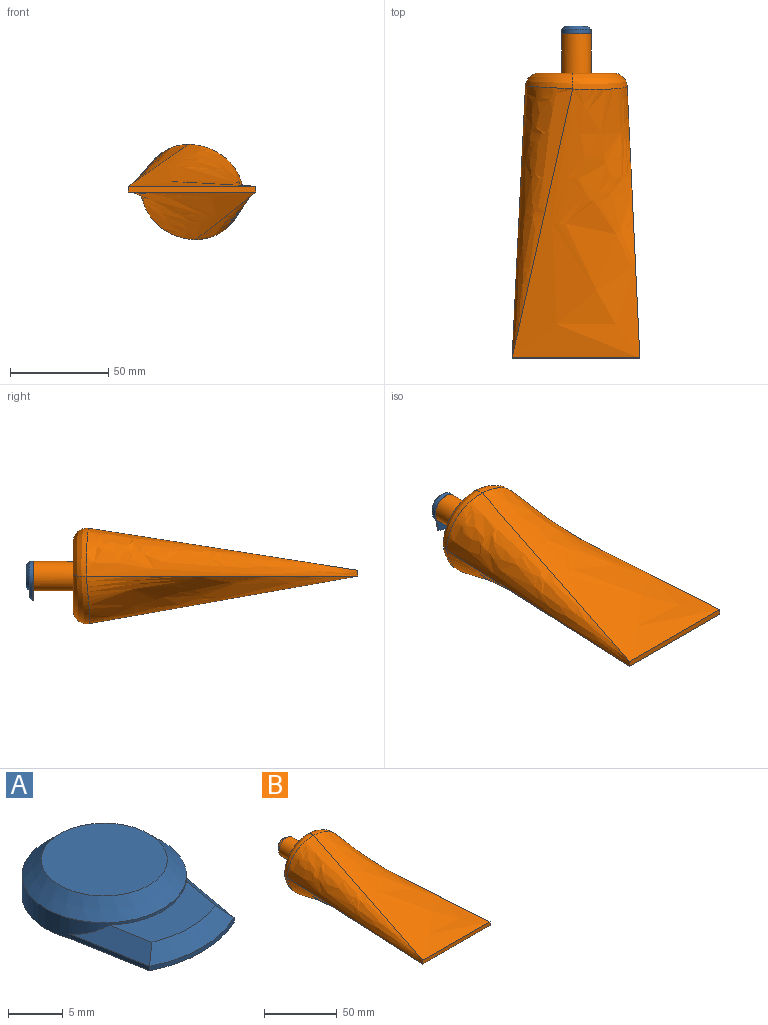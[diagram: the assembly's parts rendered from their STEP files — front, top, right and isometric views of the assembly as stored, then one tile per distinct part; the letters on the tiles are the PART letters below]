
ASSEMBLY  parts=2 mates=1
PART A: 12 faces, bbox 15x20.1x4 mm
  f0: cylinder r=7.5mm len=15mm, axis (0,0,-1), area 97.4mm2, adj f2,f3,f4,f5,f7,f8,f10,f11
  f1: plane 11.5x11.5mm, normal (0,0,1), area 103.9mm2, adj f11
  f2: plane 20.12x15mm, normal (0,0,-1), area 244.3mm2, adj f0,f3,f4,f5,f6
  f3: plane 8.8x1.55mm, normal (-0.98,-0.17,0), area 4.5mm2, adj f0,f2,f6,f10
  f4: plane 8.28x1.46mm, normal (0.98,-0.17,0), area 4.2mm2, adj f0,f2,f6,f8
  f5: cylinder r=7.39mm len=9.81mm, axis (0,0,-1), area 20.9mm2, adj f0,f2,f7,f10
  f6: cylinder r=12.21mm len=10.9mm, axis (0,0,-1), area 5.6mm2, adj f2,f3,f4,f9
  f7: plane 9.84x5.47mm, normal (0,0,1), area 33.7mm2, adj f0,f5,f8,f9,f10
  f8: plane 8.28x2.8mm, normal (0.7,-0.12,0.71), area 13.3mm2, adj f0,f4,f7,f9
  f9: cone r=10.71mm half-angle=45deg, axis (0,0,-1), area 20.9mm2, adj f6,f7,f8,f10
  f10: plane 8.81x2.9mm, normal (-0.7,-0.12,0.71), area 13.7mm2, adj f0,f3,f5,f7,f9
  f11: cone r=5.75mm half-angle=45deg, axis (0,0,-1), area 103mm2, adj f0,f1
PART B: 16 faces, bbox 65x168x51.2 mm
  f0: plane 65x3mm, normal (0,-1,0), area 195mm2, adj f2,f3,f4,f5
  f1: plane 37.79x34.63mm, normal (0,1,0), area 833.4mm2, adj f6,f7,f8,f9,f10
  f2: bspline ~138.34x31.14mm, area 2790.3mm2, adj f0,f3,f5,f6,f8,f9
  f3: bspline ~145x65mm, area 6889mm2, adj f0,f2,f4,f6,f7
  f4: bspline ~138.33x30.87mm, area 2788.2mm2, adj f0,f3,f5,f7,f9
  f5: bspline ~145x65mm, area 6921.7mm2, adj f0,f2,f4,f9
  f6: bspline ~27.94x26.51mm, area 436.7mm2, adj f1,f2,f3,f7,f8
  f7: bspline ~26.04x24.17mm, area 383mm2, adj f1,f3,f4,f6,f9
  f8: bspline ~25.93x24.22mm, area 379.1mm2, adj f1,f2,f6,f9
  f9: bspline ~28.1x26.5mm, area 440.2mm2, adj f1,f2,f4,f5,f7,f8
  f10: cylinder r=7.5mm len=20mm, axis (0,-1,0), area 942.5mm2, adj f1,f11
  f11: plane 15x15mm, normal (0,1,0), area 89.3mm2, adj f10,f12
  f12: cylinder r=5.28mm len=10.55mm, axis (0,-1,0), area 99.4mm2, adj f11,f13
  f13: plane 10.55x10.55mm, normal (0,1,0), area 25.3mm2, adj f12,f14
  f14: cylinder r=4.45mm len=8.89mm, axis (0,1,0), area 83.8mm2, adj f13,f15
  f15: plane 8.89x8.89mm, normal (0,1,0), area 62.1mm2, adj f14
PLACE A rot(axis=(0,0.71,0.71),180deg) t=(-35.37,56.24,-6.39)mm
PLACE B t=(-35.37,-34.76,-6.39)mm
MATE fastened A.f0 <-> B.f10  axis (0,-1,0) through (-35.37,56.24,-6.39)mm
